# Revit family: Aeon
name_source: partatom
category: Мебель
revit_build: Autodesk Revit 2017 (Build: 20160225_1515(x64)
units: mm (PartAtom-declared; Revit-internal decimal feet)

## family parameters
Всегда вертикально = Да
Заголовок OmniClass = General Furniture and Specialties
На основе рабочей плоскости = Нет
Номер OmniClass = 23.40.20.00
Общий = Нет
При загрузке вырезать с полостями = Нет
Точка расчета площади = Нет

## types (2) — shared parameters
Legs Material = Skandiform Chrome
Table Top Material = Skandiform  Wood Oak Veneer
Изготовитель = Skandiform AB
Ключевая пометка = XBE.1
Комментарии к типоразмеру = Created by Astacus AB

## per-type parameters (varying)
| type | URL | Width |
| LB-780 | http://file-system.ru | 660 мм |
| LB-781 | www.biminfo.se/?productid=333353 | 1060 мм |

note: column(s) folded — value = type name in every type: Leg, Группа модели

## geometry (parser evidence)
native form markers: Blend x12, Sweep x8
no freeform markers — native parametric forms only
